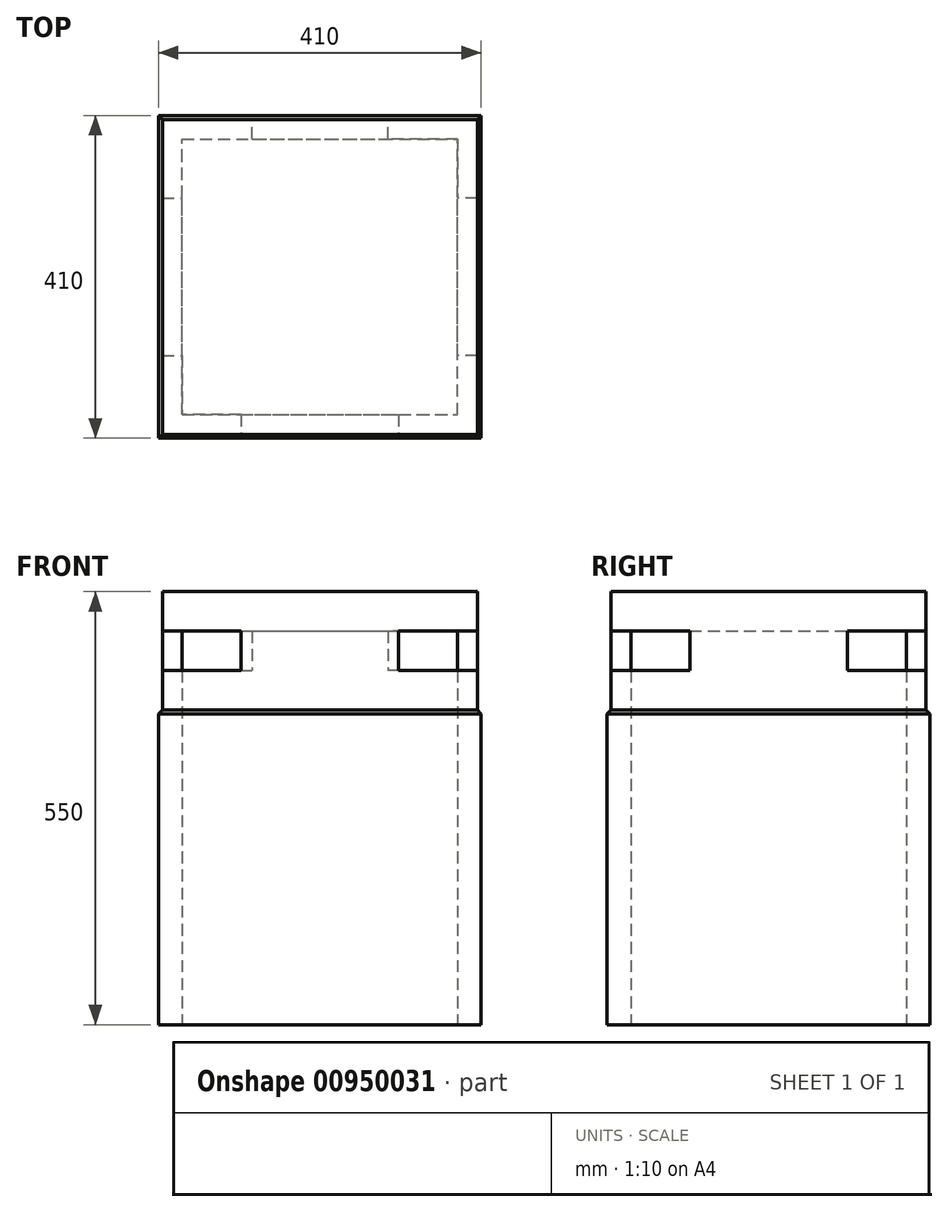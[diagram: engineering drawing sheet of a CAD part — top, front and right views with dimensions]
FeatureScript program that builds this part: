
annotation { "Feature Type Name" : "Feature", "Feature Type Description" : "" }
export const myFeature = defineFeature(function(context is Context, id is Id, definition is map)
    precondition{}
    {
        {
            var Q0;
            Q0=qCreatedBy(makeId("Top.planeOp"),FACE);
            var sketch = newSketch(context, id + "F0", { "sketchPlane" : qUnion([Q0])});
            skLineSegment(sketch, "E0.bottom", {"start": v(200, -200) * mm, "end": v(-200, -200) * mm});
            skLineSegment(sketch, "E0.top", {"start": v(200, 200) * mm, "end": v(-200, 200) * mm});
            skLineSegment(sketch, "E0.left", {"start": v(200, -200) * mm, "end": v(200, 200) * mm});
            skLineSegment(sketch, "E0.right", {"start": v(-200, -200) * mm, "end": v(-200, 200) * mm});
            skPoint(sketch, "E0.middle", {"position": v(0, 0) * mm});
            skSolve(sketch);
        }
        {
            var Q0;
            Q0=makeQuery(id+"F0.imprint","IMPRINT",FACE,{"disambiguationData":[TD([[makeQuery(id+"F0.imprint","IMPRINT",EDGE,{"derivedFrom":sQuery(id+"F0.wireOp",EDGE,"E0.bottom")}),-1.0]])]});
            var Q1;
            Q1=sQuery(id+"F0.wireOp",EDGE,"E0.bottom");
            var Q2;
            Q2=sQuery(id+"F0.wireOp",EDGE,"E0.right");
            var Q3;
            Q3=sQuery(id+"F0.wireOp",EDGE,"E0.top");
            var Q4;
            Q4=sQuery(id+"F0.wireOp",EDGE,"E0.left");
            extrude(context, id + "F1", {"entities" : qUnion([Q0]), "surfaceEntities" : qUnion([Q1, Q2, Q3, Q4]), "depth" : 150 * mm, "offsetDistance" : 25 * mm});
        }
        {
            var Q0;
            Q0=makeQuery(id+"F0.imprint","IMPRINT",FACE,{"disambiguationData":[TD([[makeQuery(id+"F0.imprint","IMPRINT",EDGE,{"derivedFrom":sQuery(id+"F0.wireOp",EDGE,"E0.bottom")}),-1.0]])]});
            var sketch = newSketch(context, id + "F2", { "sketchPlane" : qUnion([Q0])});
            skLineSegment(sketch, "E1.bottom", {"start": v(-205, 205) * mm, "end": v(205, 205) * mm});
            skLineSegment(sketch, "E1.top", {"start": v(-205, -205) * mm, "end": v(205, -205) * mm});
            skLineSegment(sketch, "E1.left", {"start": v(-205, 205) * mm, "end": v(-205, -205) * mm});
            skLineSegment(sketch, "E1.right", {"start": v(205, 205) * mm, "end": v(205, -205) * mm});
            skPoint(sketch, "E1.middle", {"position": v(0, 0) * mm});
            skSolve(sketch);
        }
        {
            var Q0;
            Q0=makeQuery(id+"F2.imprint","IMPRINT",FACE,{"disambiguationData":[TD([[makeQuery(id+"F2.imprint","IMPRINT",EDGE,{"derivedFrom":sQuery(id+"F2.wireOp",EDGE,"E1.bottom")}),-1.0]])]});
            var Q1;
            Q1=makeQuery(id+"F2.imprint","IMPRINT",FACE,{"disambiguationData":[TD([[makeQuery(id+"F2.imprint","IMPRINT",EDGE,{"derivedFrom":makeQuery(id+"F0.imprint","IMPRINT",EDGE,{"derivedFrom":sQuery(id+"F0.wireOp",EDGE,"E0.bottom")})}),-1.0]])]});
            extrude(context, id + "F3", {"entities" : qUnion([Q0, Q1]), "operationType" : NewBodyOperationType.ADD, "oppositeDirection" : true, "depth" : 400 * mm, "offsetDistance" : 25 * mm});
        }
        {
            var Q0;
            Q0=makeQuery(id+"F3.opExtrude","CAP_FACE",FACE,{"disambiguationData":[OSD([sQuery(id+"F2.wireOp",EDGE,"E1.bottom"),sQuery(id+"F2.wireOp",EDGE,"E1.top"),sQuery(id+"F2.wireOp",EDGE,"E1.left"),sQuery(id+"F2.wireOp",EDGE,"E1.right")])],"isStart":false});
            var sketch = newSketch(context, id + "F4", { "sketchPlane" : qUnion([Q0])});
            skLineSegment(sketch, "E2.bottom", {"start": v(-175, 175) * mm, "end": v(175, 175) * mm});
            skLineSegment(sketch, "E2.top", {"start": v(-175, -175) * mm, "end": v(175, -175) * mm});
            skLineSegment(sketch, "E2.left", {"start": v(-175, 175) * mm, "end": v(-175, -175) * mm});
            skLineSegment(sketch, "E2.right", {"start": v(175, 175) * mm, "end": v(175, -175) * mm});
            skPoint(sketch, "E2.middle", {"position": v(0, 0) * mm});
            skSolve(sketch);
        }
        {
            var Q0;
            Q0=makeQuery(id+"F4.imprint","IMPRINT",FACE,{"disambiguationData":[TD([[makeQuery(id+"F4.imprint","IMPRINT",EDGE,{"derivedFrom":sQuery(id+"F4.wireOp",EDGE,"E2.bottom")}),-1.0]])]});
            extrude(context, id + "F5", {"entities" : qUnion([Q0]), "operationType" : NewBodyOperationType.REMOVE, "oppositeDirection" : true, "depth" : 500 * mm, "offsetDistance" : 25 * mm});
        }
        {
            var Q0;
            Q0=makeQuery(id+"F1.opExtrude","SWEPT_FACE",FACE,{"disambiguationData":[OSD([sQuery(id+"F0.wireOp",EDGE,"E0.bottom")])]});
            var sketch = newSketch(context, id + "F6", { "sketchPlane" : qUnion([Q0])});
            skLineSegment(sketch, "E3.bottom", {"start": v(200, 100) * mm, "end": v(100, 100) * mm});
            skLineSegment(sketch, "E3.top", {"start": v(200, 50) * mm, "end": v(100, 50) * mm});
            skLineSegment(sketch, "E3.left", {"start": v(200, 100) * mm, "end": v(200, 50) * mm});
            skLineSegment(sketch, "E3.right", {"start": v(100, 100) * mm, "end": v(100, 50) * mm});
            skLineSegment(sketch, "E4.bottom", {"start": v(-200, 100) * mm, "end": v(-100, 100) * mm});
            skLineSegment(sketch, "E4.top", {"start": v(-200, 50) * mm, "end": v(-100, 50) * mm});
            skLineSegment(sketch, "E4.left", {"start": v(-200, 100) * mm, "end": v(-200, 50) * mm});
            skLineSegment(sketch, "E4.right", {"start": v(-100, 100) * mm, "end": v(-100, 50) * mm});
            skSolve(sketch);
        }
        {
            var Q0;
            Q0=makeQuery(id+"F6.imprint","IMPRINT",FACE,{"disambiguationData":[TD([[makeQuery(id+"F6.imprint","IMPRINT",EDGE,{"derivedFrom":sQuery(id+"F6.wireOp",EDGE,"E3.bottom")}),1.0]])]});
            var Q1;
            Q1=makeQuery(id+"F6.imprint","IMPRINT",FACE,{"disambiguationData":[TD([[makeQuery(id+"F6.imprint","IMPRINT",EDGE,{"derivedFrom":sQuery(id+"F6.wireOp",EDGE,"E4.bottom")}),-1.0]])]});
            extrude(context, id + "F7", {"entities" : qUnion([Q0, Q1]), "operationType" : NewBodyOperationType.REMOVE, "oppositeDirection" : true, "depth" : 100 * mm, "offsetDistance" : 25 * mm});
        }
        {
            var Q0;
            Q0=makeQuery(id+"F1.opExtrude","SWEPT_FACE",FACE,{"disambiguationData":[OSD([sQuery(id+"F0.wireOp",EDGE,"E0.top")])]});
            var sketch = newSketch(context, id + "F8", { "sketchPlane" : qUnion([Q0])});
            skLineSegment(sketch, "E5.bottom", {"start": v(200, 100) * mm, "end": v(86.32, 100) * mm});
            skLineSegment(sketch, "E5.top", {"start": v(200, 50) * mm, "end": v(86.32, 50) * mm});
            skLineSegment(sketch, "E5.left", {"start": v(200, 100) * mm, "end": v(200, 50) * mm});
            skLineSegment(sketch, "E5.right", {"start": v(86.32, 100) * mm, "end": v(86.32, 50) * mm});
            skLineSegment(sketch, "E6.bottom", {"start": v(-200, 100) * mm, "end": v(-86.32, 100) * mm});
            skLineSegment(sketch, "E6.top", {"start": v(-200, 50) * mm, "end": v(-86.32, 50) * mm});
            skLineSegment(sketch, "E6.left", {"start": v(-200, 100) * mm, "end": v(-200, 50) * mm});
            skLineSegment(sketch, "E6.right", {"start": v(-86.32, 100) * mm, "end": v(-86.32, 50) * mm});
            skSolve(sketch);
        }
        {
            var Q0;
            Q0=makeQuery(id+"F8.imprint","IMPRINT",FACE,{"disambiguationData":[TD([[makeQuery(id+"F8.imprint","IMPRINT",EDGE,{"derivedFrom":sQuery(id+"F8.wireOp",EDGE,"E6.bottom")}),-1.0]])]});
            var Q1;
            Q1=makeQuery(id+"F8.imprint","IMPRINT",FACE,{"disambiguationData":[TD([[makeQuery(id+"F8.imprint","IMPRINT",EDGE,{"derivedFrom":sQuery(id+"F8.wireOp",EDGE,"E5.bottom")}),1.0]])]});
            extrude(context, id + "F9", {"entities" : qUnion([Q0, Q1]), "operationType" : NewBodyOperationType.REMOVE, "oppositeDirection" : true, "depth" : 100 * mm, "offsetDistance" : 25 * mm});
        }
        {
            var Q0;
            Q0=makeQuery(id+"F3.opExtrude","CAP_EDGE",EDGE,{"disambiguationData":[OSD([sQuery(id+"F2.wireOp",EDGE,"E1.top")])],"isStart":true});
            var Q1;
            Q1=makeQuery(id+"F3.opExtrude","CAP_EDGE",EDGE,{"disambiguationData":[OSD([sQuery(id+"F2.wireOp",EDGE,"E1.left")])],"isStart":true});
            var Q2;
            Q2=makeQuery(id+"F3.opExtrude","CAP_EDGE",EDGE,{"disambiguationData":[OSD([sQuery(id+"F2.wireOp",EDGE,"E1.bottom")])],"isStart":true});
            var Q3;
            Q3=makeQuery(id+"F3.opExtrude","CAP_EDGE",EDGE,{"disambiguationData":[OSD([sQuery(id+"F2.wireOp",EDGE,"E1.right")])],"isStart":true});
            chamfer(context, id + "F10", {"entities" : qUnion([Q0, Q1, Q2, Q3]), "width" : 5 * mm, "tangentPropagation" : true});
        }
    });
